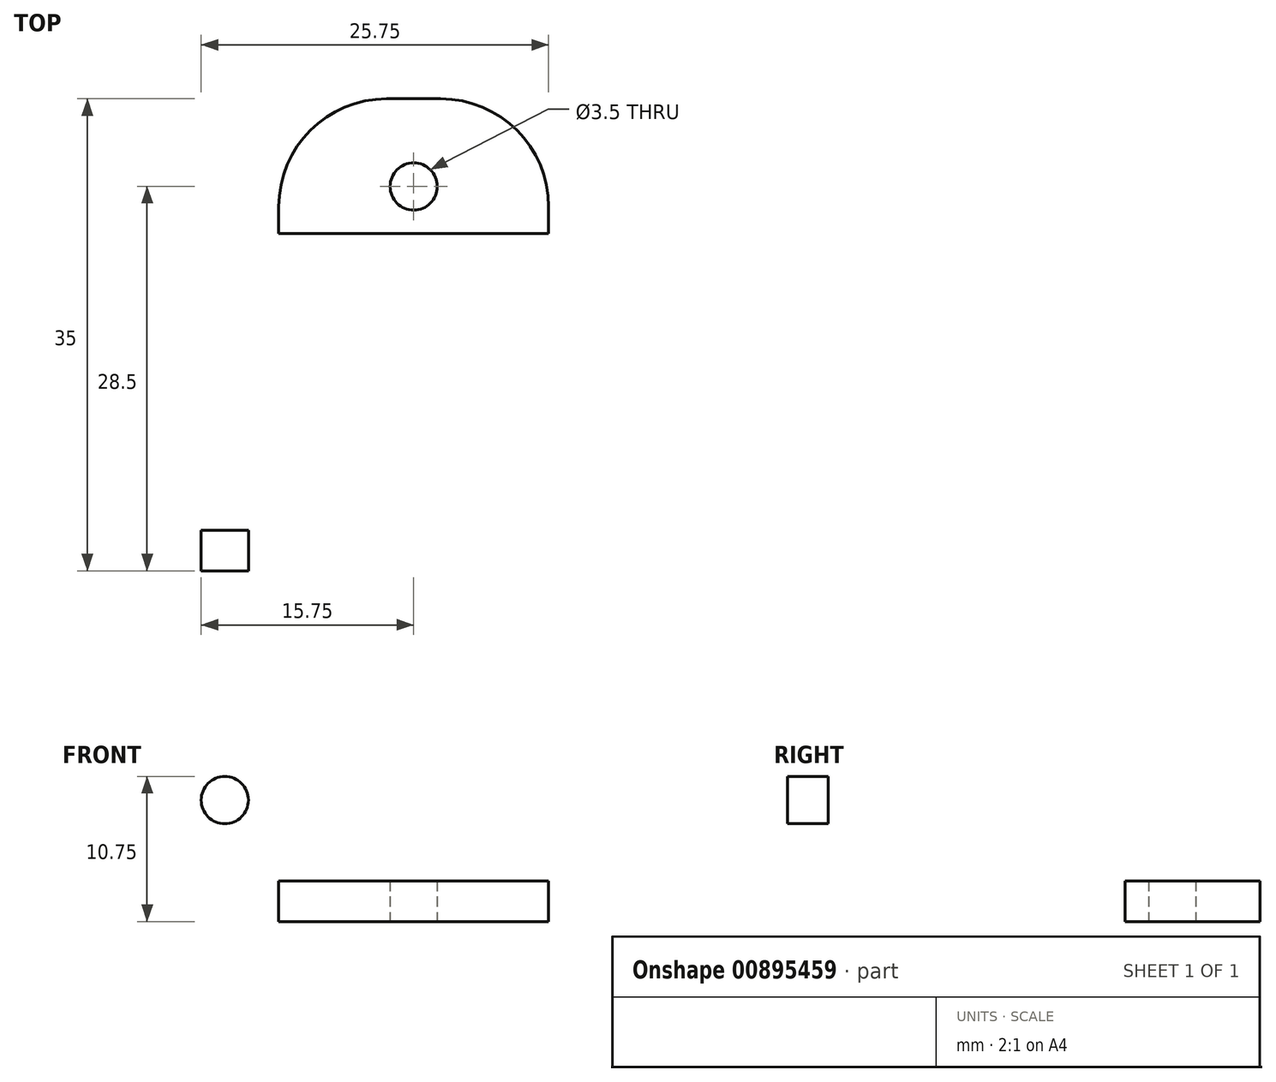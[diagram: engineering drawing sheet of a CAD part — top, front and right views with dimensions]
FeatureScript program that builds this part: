
annotation { "Feature Type Name" : "Feature", "Feature Type Description" : "" }
export const myFeature = defineFeature(function(context is Context, id is Id, definition is map)
    precondition{}
    {
        {
            var Q0;
            Q0=qCreatedBy(makeId("Top.planeOp"),FACE);
            var sketch = newSketch(context, id + "F0", { "sketchPlane" : qUnion([Q0])});
            skLineSegment(sketch, "E0.bottom", {"start": v(2, 17.5) * mm, "end": v(-2, 17.5) * mm});
            skLineSegment(sketch, "E0.top", {"start": v(10, -17.5) * mm, "end": v(-10, -17.5) * mm});
            skLineSegment(sketch, "E0.right", {"start": v(-10, 9.5) * mm, "end": v(-10, 6.05) * mm});
            skPoint(sketch, "E0.middle", {"position": v(0, 0) * mm});
            skPoint(sketch, "E1", {"position": v(0, 11) * mm});
            skCircle(sketch, "E2", {"center": v(0, 11) * mm, "radius": 1.75 * mm});
            skPoint(sketch, "E3.visualSharp", {"position": v(10, 17.5) * mm});
            skArc(sketch, "E3.filletArc", {"start": v(10, 9.5) * mm, "mid": v(7.66, 15.16) * mm, "end": v(2, 17.5) * mm});
            skPoint(sketch, "E4.visualSharp", {"position": v(-10, 17.5) * mm});
            skArc(sketch, "E4.filletArc", {"start": v(-2, 17.5) * mm, "mid": v(-7.66, 15.16) * mm, "end": v(-10, 9.5) * mm});
            skLineSegment(sketch, "E5", {"start": v(-10, -17.5) * mm, "end": v(-20, -17.5) * mm});
            skPoint(sketch, "E6.newPointA", {"position": v(-7.37, 0) * mm});
            skArc(sketch, "E6.filletArc", {"start": v(-15.68, -11.5) * mm, "mid": v(-11.45, -3.18) * mm, "end": v(-10, 6.05) * mm});
            skArc(sketch, "E7.MirrorCS", {"start": v(15.68, -11.5) * mm, "mid": v(11.45, -3.18) * mm, "end": v(10, 6.05) * mm});
            skLineSegment(sketch, "E8.MirrorCS", {"start": v(10, -17.5) * mm, "end": v(20, -17.5) * mm});
            skLineSegment(sketch, "E9", {"start": v(-20, -17.5) * mm, "end": v(-20, -14.5) * mm});
            skLineSegment(sketch, "E10", {"start": v(-20, -14.5) * mm, "end": v(20, -14.5) * mm});
            skLineSegment(sketch, "E11", {"start": v(20, -14.5) * mm, "end": v(20, -17.5) * mm});
            skLineSegment(sketch, "E12", {"start": v(-15.68, -11.5) * mm, "end": v(-20, -14.5) * mm});
            skLineSegment(sketch, "E13", {"start": v(15.68, -11.5) * mm, "end": v(20, -14.5) * mm});
            skLineSegment(sketch, "E14.bottom", {"start": v(-1.8, 2.5) * mm, "end": v(1.8, 2.5) * mm});
            skLineSegment(sketch, "E14.top", {"start": v(-1.8, -17.5) * mm, "end": v(1.8, -17.5) * mm});
            skLineSegment(sketch, "E14.left", {"start": v(-1.8, 2.5) * mm, "end": v(-1.8, -17.5) * mm});
            skLineSegment(sketch, "E14.right", {"start": v(1.8, 2.5) * mm, "end": v(1.8, -17.5) * mm});
            skPoint(sketch, "E14.middle", {"position": v(0, -7.5) * mm});
            skLineSegment(sketch, "E15", {"start": v(10, 6.05) * mm, "end": v(10, 9.5) * mm});
            skSolve(sketch);
        }
        {
            var Q0;
            {var subQ4=sQuery(id+"F0.wireOp",EDGE,"E5");Q0=makeQuery(id+"F0.imprint","IMPRINT",FACE,{"disambiguationData":[TD([[makeQuery(id+"F0.imprint","IMPRINT",EDGE,{"derivedFrom":subQ4}),-1.0]])]});}
            var Q1;
            {var subQ0=sQuery(id+"F0.wireOp",EDGE,"E14.left");var subQ1=sQuery(id+"F0.wireOp",EDGE,"E0.top");var subQ2=makeQuery(id+"F0.imprint","INTERSECT",VERTEX,{"derivedFrom":[subQ1,subQ0]});Q1=makeQuery(id+"F0.imprint","IMPRINT",FACE,{"disambiguationData":[TD([[makeQuery(id+"F0.imprint","IMPRINT",EDGE,{"disambiguationData":[TD([[subQ2,1.0]])],"derivedFrom":subQ1}),-1.0]])]});}
            var Q2;
            {var subQ4=sQuery(id+"F0.wireOp",EDGE,"E8.MirrorCS");Q2=makeQuery(id+"F0.imprint","IMPRINT",FACE,{"disambiguationData":[TD([[makeQuery(id+"F0.imprint","IMPRINT",EDGE,{"derivedFrom":subQ4}),1.0]])]});}
            var Q3;
            {var subQ5=sQuery(id+"F0.wireOp",EDGE,"E14.bottom");Q3=makeQuery(id+"F0.imprint","IMPRINT",FACE,{"disambiguationData":[TD([[makeQuery(id+"F0.imprint","IMPRINT",EDGE,{"derivedFrom":subQ5}),-1.0]])]});}
            extrude(context, id + "F1", {"entities" : qUnion([Q0, Q1, Q2, Q3]), "depth" : 15 * mm, "offsetDistance" : 25 * mm});
        }
        {
            var Q0;
            Q0=makeQuery(id+"F0.imprint","IMPRINT",FACE,{"disambiguationData":[TD([[makeQuery(id+"F0.imprint","IMPRINT",EDGE,{"derivedFrom":sQuery(id+"F0.wireOp",EDGE,"E0.bottom")}),1.0]])]});
            extrude(context, id + "F2", {"entities" : qUnion([Q0]), "operationType" : NewBodyOperationType.ADD, "depth" : 3 * mm, "offsetDistance" : 25 * mm});
        }
        {
            var Q0;
            Q0=makeQuery(id+"F1.opExtrude","SWEPT_FACE",FACE,{"disambiguationData":[OSD([sQuery(id+"F0.wireOp",EDGE,"E14.right")])]});
            var sketch = newSketch(context, id + "F3", { "sketchPlane" : qUnion([Q0])});
            skLineSegment(sketch, "E16", {"start": v(-14.5, 15) * mm, "end": v(2.5, 3) * mm});
            skLineSegment(sketch, "E17", {"start": v(2.5, 3) * mm, "end": v(2.5, 15) * mm});
            skLineSegment(sketch, "E18", {"start": v(2.5, 15) * mm, "end": v(-14.5, 15) * mm});
            skSolve(sketch);
        }
        {
            var Q0;
            Q0=makeQuery(id+"F3.imprint","IMPRINT",FACE,{"disambiguationData":[TD([[makeQuery(id+"F3.imprint","IMPRINT",EDGE,{"derivedFrom":sQuery(id+"F3.wireOp",EDGE,"E16")}),1.0]])]});
            extrude(context, id + "F4", {"entities" : qUnion([Q0]), "operationType" : NewBodyOperationType.REMOVE, "oppositeDirection" : true, "depth" : 25 * mm, "offsetDistance" : 25 * mm});
        }
        {
            var Q0;
            Q0=makeQuery(id+"F1.opExtrude","SWEPT_FACE",FACE,{"disambiguationData":[OSD([sQuery(id+"F0.wireOp",EDGE,"E0.top"),sQuery(id+"F0.wireOp",EDGE,"E5"),sQuery(id+"F0.wireOp",EDGE,"E8.MirrorCS")])]});
            var sketch = newSketch(context, id + "F5", { "sketchPlane" : qUnion([Q0])});
            skCircle(sketch, "E19", {"center": v(14, 9) * mm, "radius": 1.75 * mm});
            skCircle(sketch, "E20.MirrorC", {"center": v(-14, 9) * mm, "radius": 1.75 * mm});
            skSolve(sketch);
        }
        {
            var Q0;
            Q0=makeQuery(id+"F5.imprint","IMPRINT",FACE,{"disambiguationData":[TD([[makeQuery(id+"F5.imprint","IMPRINT",EDGE,{"derivedFrom":sQuery(id+"F5.wireOp",EDGE,"E19")}),1.0]])]});
            var Q1;
            Q1=makeQuery(id+"F5.imprint","IMPRINT",FACE,{"disambiguationData":[TD([[makeQuery(id+"F5.imprint","IMPRINT",EDGE,{"derivedFrom":sQuery(id+"F5.wireOp",EDGE,"E20.MirrorC")}),-1.0]])]});
            extrude(context, id + "F6", {"entities" : qUnion([Q0, Q1]), "operationType" : NewBodyOperationType.REMOVE, "oppositeDirection" : true, "depth" : 25 * mm, "offsetDistance" : 25 * mm});
        }
    });
